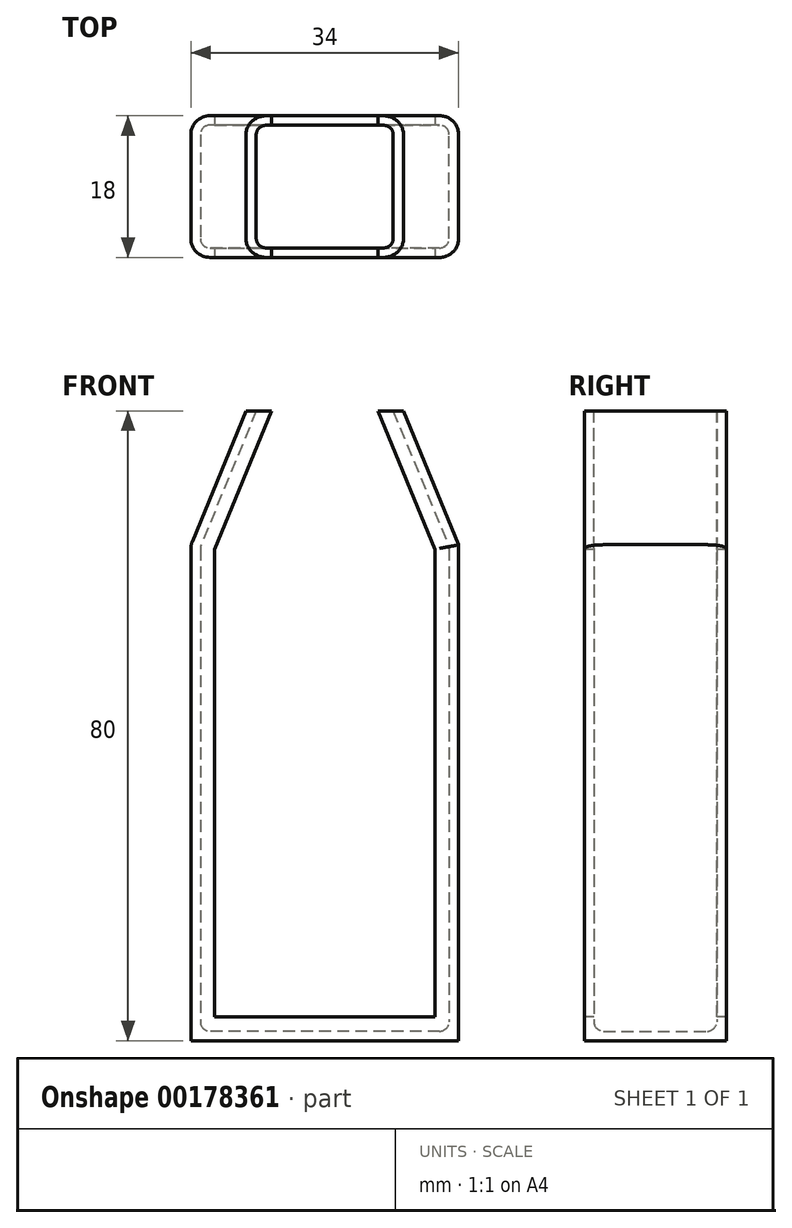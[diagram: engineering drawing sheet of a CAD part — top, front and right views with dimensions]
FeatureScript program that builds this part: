
annotation { "Feature Type Name" : "Feature", "Feature Type Description" : "" }
export const myFeature = defineFeature(function(context is Context, id is Id, definition is map)
    precondition{}
    {
        {
            var Q0;
            Q0=qCreatedBy(makeId("Top.planeOp"),FACE);
            var sketch = newSketch(context, id + "F0", { "sketchPlane" : qUnion([Q0])});
            skLineSegment(sketch, "E0.bottom", {"start": v(17, -9) * mm, "end": v(-17, -9) * mm});
            skLineSegment(sketch, "E0.top", {"start": v(17, 9) * mm, "end": v(-17, 9) * mm});
            skLineSegment(sketch, "E0.left", {"start": v(17, -9) * mm, "end": v(17, 9) * mm});
            skLineSegment(sketch, "E0.right", {"start": v(-17, -9) * mm, "end": v(-17, 9) * mm});
            skPoint(sketch, "E0.middle", {"position": v(0, 0) * mm});
            skSolve(sketch);
        }
        {
            var Q0;
            Q0=makeQuery(id+"F0.imprint","IMPRINT",FACE,{"disambiguationData":[TD([[makeQuery(id+"F0.imprint","IMPRINT",EDGE,{"derivedFrom":sQuery(id+"F0.wireOp",EDGE,"E0.bottom")}),-1.0]])]});
            extrude(context, id + "F1", {"entities" : qUnion([Q0]), "depth" : 80 * mm});
        }
        {
            var Q0;
            Q0=makeQuery(id+"F1.opExtrude","CAP_EDGE",EDGE,{"disambiguationData":[OSD([sQuery(id+"F0.wireOp",EDGE,"E0.right")])],"isStart":false});
            var Q1;
            Q1=makeQuery(id+"F1.opExtrude","CAP_EDGE",EDGE,{"disambiguationData":[OSD([sQuery(id+"F0.wireOp",EDGE,"E0.left")])],"isStart":false});
            chamfer(context, id + "F2", {"entities" : qUnion([Q0, Q1]), "chamferType" : ChamferType.TWO_OFFSETS, "width1" : 17 * mm, "oppositeDirection" : false, "width2" : 7 * mm, "tangentPropagation" : true});
        }
        {
            var Q0;
            Q0=makeQuery(id+"F1.opExtrude","CAP_FACE",FACE,{"disambiguationData":[OSD([sQuery(id+"F0.wireOp",EDGE,"E0.bottom"),sQuery(id+"F0.wireOp",EDGE,"E0.top"),sQuery(id+"F0.wireOp",EDGE,"E0.left"),sQuery(id+"F0.wireOp",EDGE,"E0.right")])],"isStart":false});
            shell(context, id + "F3", {"entities" : qUnion([Q0]), "thickness" : 1.2 * mm});
        }
        {
            var Q0;
            Q0=makeQuery(id+"F1.opExtrude","SWEPT_FACE",FACE,{"disambiguationData":[OSD([sQuery(id+"F0.wireOp",EDGE,"E0.bottom")])]});
            var sketch = newSketch(context, id + "F4", { "sketchPlane" : qUnion([Q0])});
            skLineSegment(sketch, "E1", {"start": v(-14, 80) * mm, "end": v(-14, 3) * mm});
            skLineSegment(sketch, "E2", {"start": v(-14, 3) * mm, "end": v(14, 3) * mm});
            skLineSegment(sketch, "E3", {"start": v(14, 3) * mm, "end": v(14, 80) * mm});
            skLineSegment(sketch, "E4", {"start": v(14, 62.4) * mm, "end": v(6.76, 80) * mm});
            skLineSegment(sketch, "E5", {"start": v(-14, 62.4) * mm, "end": v(-6.76, 80) * mm});
            skSolve(sketch);
        }
        {
            var Q0;
            {var subQ2=sQuery(id+"F4.wireOp",EDGE,"E2");Q0=makeQuery(id+"F4.imprint","IMPRINT",FACE,{"disambiguationData":[TD([[makeQuery(id+"F4.imprint","IMPRINT",EDGE,{"derivedFrom":subQ2}),1.0]])]});}
            extrude(context, id + "F5", {"entities" : qUnion([Q0]), "operationType" : NewBodyOperationType.REMOVE, "endBound" : BoundingType.THROUGH_ALL, "oppositeDirection" : true, "depth" : 1.2 * mm});
        }
        {
            var Q0;
            {var subQ0=sQuery(id+"F0.wireOp",EDGE,"E0.top");Q0=makeQuery(id+"F3.opShell","OFFSET_EDGE",EDGE,{"disambiguationData":[OSD([subQ0]),TDD([makeQuery(id+"F1.opExtrude","CAP_EDGE",EDGE,{"disambiguationData":[OSD([subQ0])],"isStart":true})])]});}
            var Q1;
            {var subQ0=sQuery(id+"F0.wireOp",EDGE,"E0.right");var subQ1=sQuery(id+"F0.wireOp",EDGE,"E0.top");Q1=makeQuery(id+"F3.opShell","OFFSET_EDGE",EDGE,{"disambiguationData":[OSD([subQ1,subQ0]),TDD([makeQuery(id+"F1.opExtrude","SWEPT_EDGE",EDGE,{"disambiguationData":[OSD([subQ1,subQ0])]})])]});}
            var Q2;
            {var subQ0=sQuery(id+"F0.wireOp",EDGE,"E0.right");var subQ1=sQuery(id+"F0.wireOp",EDGE,"E0.bottom");Q2=makeQuery(id+"F3.opShell","OFFSET_EDGE",EDGE,{"disambiguationData":[OSD([subQ1,subQ0]),TDD([makeQuery(id+"F1.opExtrude","SWEPT_EDGE",EDGE,{"disambiguationData":[OSD([subQ1,subQ0])]})])]});}
            var Q3;
            {var subQ0=sQuery(id+"F0.wireOp",EDGE,"E0.top");var subQ1=sQuery(id+"F0.wireOp",EDGE,"E0.right");Q3=makeQuery(id+"F3.opShell","OFFSET_EDGE",EDGE,{"disambiguationData":[OSD([subQ0,subQ1]),TDD([makeQuery(id+"F2.opChamfer","BLEND_EDGE",EDGE,{"blendedFrom":[makeQuery(id+"F1.opExtrude","CAP_EDGE",EDGE,{"disambiguationData":[OSD([subQ1])],"isStart":false}),makeQuery(id+"F1.opExtrude","SWEPT_FACE",FACE,{"disambiguationData":[OSD([subQ0])]})],"blendedInto":[makeQuery(id+"F1.opExtrude","SWEPT_FACE",FACE,{"disambiguationData":[OSD([subQ0])]})]})])]});}
            var Q4;
            {var subQ0=sQuery(id+"F0.wireOp",EDGE,"E0.bottom");var subQ1=sQuery(id+"F0.wireOp",EDGE,"E0.right");Q4=makeQuery(id+"F3.opShell","OFFSET_EDGE",EDGE,{"disambiguationData":[OSD([subQ0,subQ1]),TDD([makeQuery(id+"F2.opChamfer","BLEND_EDGE",EDGE,{"blendedFrom":[makeQuery(id+"F1.opExtrude","CAP_EDGE",EDGE,{"disambiguationData":[OSD([subQ1])],"isStart":false}),makeQuery(id+"F1.opExtrude","SWEPT_FACE",FACE,{"disambiguationData":[OSD([subQ0])]})],"blendedInto":[makeQuery(id+"F1.opExtrude","SWEPT_FACE",FACE,{"disambiguationData":[OSD([subQ0])]})]})])]});}
            var Q5;
            {var subQ0=sQuery(id+"F0.wireOp",EDGE,"E0.left");var subQ1=sQuery(id+"F0.wireOp",EDGE,"E0.bottom");Q5=makeQuery(id+"F3.opShell","OFFSET_EDGE",EDGE,{"disambiguationData":[OSD([subQ1,subQ0]),TDD([makeQuery(id+"F1.opExtrude","SWEPT_EDGE",EDGE,{"disambiguationData":[OSD([subQ1,subQ0])]})])]});}
            var Q6;
            {var subQ0=sQuery(id+"F0.wireOp",EDGE,"E0.bottom");var subQ1=sQuery(id+"F0.wireOp",EDGE,"E0.left");Q6=makeQuery(id+"F3.opShell","OFFSET_EDGE",EDGE,{"disambiguationData":[OSD([subQ0,subQ1]),TDD([makeQuery(id+"F2.opChamfer","BLEND_EDGE",EDGE,{"blendedFrom":[makeQuery(id+"F1.opExtrude","CAP_EDGE",EDGE,{"disambiguationData":[OSD([subQ1])],"isStart":false}),makeQuery(id+"F1.opExtrude","SWEPT_FACE",FACE,{"disambiguationData":[OSD([subQ0])]})],"blendedInto":[makeQuery(id+"F1.opExtrude","SWEPT_FACE",FACE,{"disambiguationData":[OSD([subQ0])]})]})])]});}
            var Q7;
            {var subQ0=sQuery(id+"F0.wireOp",EDGE,"E0.left");Q7=makeQuery(id+"F3.opShell","OFFSET_EDGE",EDGE,{"disambiguationData":[OSD([subQ0]),TDD([makeQuery(id+"F2.opChamfer","BLEND_EDGE",EDGE,{"blendedFrom":[makeQuery(id+"F1.opExtrude","CAP_EDGE",EDGE,{"disambiguationData":[OSD([subQ0])],"isStart":false}),makeQuery(id+"F1.opExtrude","SWEPT_FACE",FACE,{"disambiguationData":[OSD([subQ0])]})],"blendedInto":[makeQuery(id+"F1.opExtrude","SWEPT_FACE",FACE,{"disambiguationData":[OSD([subQ0])]})]})])]});}
            var Q8;
            {var subQ0=sQuery(id+"F0.wireOp",EDGE,"E0.left");var subQ1=sQuery(id+"F0.wireOp",EDGE,"E0.top");Q8=makeQuery(id+"F3.opShell","OFFSET_EDGE",EDGE,{"disambiguationData":[OSD([subQ1,subQ0]),TDD([makeQuery(id+"F1.opExtrude","SWEPT_EDGE",EDGE,{"disambiguationData":[OSD([subQ1,subQ0])]})])]});}
            var Q9;
            {var subQ0=sQuery(id+"F0.wireOp",EDGE,"E0.top");var subQ1=sQuery(id+"F0.wireOp",EDGE,"E0.left");Q9=makeQuery(id+"F3.opShell","OFFSET_EDGE",EDGE,{"disambiguationData":[OSD([subQ0,subQ1]),TDD([makeQuery(id+"F2.opChamfer","BLEND_EDGE",EDGE,{"blendedFrom":[makeQuery(id+"F1.opExtrude","CAP_EDGE",EDGE,{"disambiguationData":[OSD([subQ1])],"isStart":false}),makeQuery(id+"F1.opExtrude","SWEPT_FACE",FACE,{"disambiguationData":[OSD([subQ0])]})],"blendedInto":[makeQuery(id+"F1.opExtrude","SWEPT_FACE",FACE,{"disambiguationData":[OSD([subQ0])]})]})])]});}
            var Q10;
            {var subQ0=sQuery(id+"F0.wireOp",EDGE,"E0.left");Q10=makeQuery(id+"F3.opShell","OFFSET_EDGE",EDGE,{"disambiguationData":[OSD([subQ0]),TDD([makeQuery(id+"F1.opExtrude","CAP_EDGE",EDGE,{"disambiguationData":[OSD([subQ0])],"isStart":true})])]});}
            var Q11;
            {var subQ0=sQuery(id+"F0.wireOp",EDGE,"E0.right");Q11=makeQuery(id+"F3.opShell","OFFSET_EDGE",EDGE,{"disambiguationData":[OSD([subQ0]),TDD([makeQuery(id+"F1.opExtrude","CAP_EDGE",EDGE,{"disambiguationData":[OSD([subQ0])],"isStart":true})])]});}
            var Q12;
            {var subQ0=sQuery(id+"F0.wireOp",EDGE,"E0.right");Q12=makeQuery(id+"F3.opShell","OFFSET_EDGE",EDGE,{"disambiguationData":[OSD([subQ0]),TDD([makeQuery(id+"F2.opChamfer","BLEND_EDGE",EDGE,{"blendedFrom":[makeQuery(id+"F1.opExtrude","CAP_EDGE",EDGE,{"disambiguationData":[OSD([subQ0])],"isStart":false}),makeQuery(id+"F1.opExtrude","SWEPT_FACE",FACE,{"disambiguationData":[OSD([subQ0])]})],"blendedInto":[makeQuery(id+"F1.opExtrude","SWEPT_FACE",FACE,{"disambiguationData":[OSD([subQ0])]})]})])]});}
            var Q13;
            {var subQ0=sQuery(id+"F0.wireOp",EDGE,"E0.bottom");Q13=makeQuery(id+"F3.opShell","OFFSET_EDGE",EDGE,{"disambiguationData":[OSD([subQ0]),TDD([makeQuery(id+"F1.opExtrude","CAP_EDGE",EDGE,{"disambiguationData":[OSD([subQ0])],"isStart":true})])]});}
            fillet(context, id + "F6", {"entities" : qUnion([Q0, Q1, Q2, Q3, Q4, Q5, Q6, Q7, Q8, Q9, Q10, Q11, Q12, Q13]), "radius" : 1.2 * mm, "tangentPropagation" : true, "allowEdgeOverflow" : false});
        }
        {
            var Q0;
            Q0=makeQuery(id+"F1.opExtrude","SWEPT_EDGE",EDGE,{"disambiguationData":[OSD([sQuery(id+"F0.wireOp",EDGE,"E0.top"),sQuery(id+"F0.wireOp",EDGE,"E0.right")])]});
            var Q1;
            Q1=makeQuery(id+"F1.opExtrude","SWEPT_EDGE",EDGE,{"disambiguationData":[OSD([sQuery(id+"F0.wireOp",EDGE,"E0.top"),sQuery(id+"F0.wireOp",EDGE,"E0.left")])]});
            var Q2;
            Q2=makeQuery(id+"F1.opExtrude","SWEPT_EDGE",EDGE,{"disambiguationData":[OSD([sQuery(id+"F0.wireOp",EDGE,"E0.bottom"),sQuery(id+"F0.wireOp",EDGE,"E0.right")])]});
            var Q3;
            Q3=makeQuery(id+"F2.opChamfer","BLEND_EDGE",EDGE,{"blendedFrom":[makeQuery(id+"F1.opExtrude","CAP_EDGE",EDGE,{"disambiguationData":[OSD([sQuery(id+"F0.wireOp",EDGE,"E0.right")])],"isStart":false}),makeQuery(id+"F1.opExtrude","SWEPT_FACE",FACE,{"disambiguationData":[OSD([sQuery(id+"F0.wireOp",EDGE,"E0.top")])]})],"blendedInto":[makeQuery(id+"F1.opExtrude","SWEPT_FACE",FACE,{"disambiguationData":[OSD([sQuery(id+"F0.wireOp",EDGE,"E0.top")])]})]});
            var Q4;
            {var subQ0=sQuery(id+"F0.wireOp",EDGE,"E0.right");Q4=makeQuery(id+"F2.opChamfer","BLEND_EDGE",EDGE,{"blendedFrom":[makeQuery(id+"F1.opExtrude","CAP_EDGE",EDGE,{"disambiguationData":[OSD([subQ0])],"isStart":false}),makeQuery(id+"F1.opExtrude","SWEPT_FACE",FACE,{"disambiguationData":[OSD([subQ0])]})],"blendedInto":[makeQuery(id+"F1.opExtrude","SWEPT_FACE",FACE,{"disambiguationData":[OSD([subQ0])]})]});}
            var Q5;
            Q5=makeQuery(id+"F2.opChamfer","BLEND_EDGE",EDGE,{"blendedFrom":[makeQuery(id+"F1.opExtrude","CAP_EDGE",EDGE,{"disambiguationData":[OSD([sQuery(id+"F0.wireOp",EDGE,"E0.right")])],"isStart":false}),makeQuery(id+"F1.opExtrude","SWEPT_FACE",FACE,{"disambiguationData":[OSD([sQuery(id+"F0.wireOp",EDGE,"E0.bottom")])]})],"blendedInto":[makeQuery(id+"F1.opExtrude","SWEPT_FACE",FACE,{"disambiguationData":[OSD([sQuery(id+"F0.wireOp",EDGE,"E0.bottom")])]})]});
            var Q6;
            Q6=makeQuery(id+"F2.opChamfer","BLEND_EDGE",EDGE,{"blendedFrom":[makeQuery(id+"F1.opExtrude","CAP_EDGE",EDGE,{"disambiguationData":[OSD([sQuery(id+"F0.wireOp",EDGE,"E0.left")])],"isStart":false}),makeQuery(id+"F1.opExtrude","SWEPT_FACE",FACE,{"disambiguationData":[OSD([sQuery(id+"F0.wireOp",EDGE,"E0.bottom")])]})],"blendedInto":[makeQuery(id+"F1.opExtrude","SWEPT_FACE",FACE,{"disambiguationData":[OSD([sQuery(id+"F0.wireOp",EDGE,"E0.bottom")])]})]});
            var Q7;
            Q7=makeQuery(id+"F1.opExtrude","SWEPT_EDGE",EDGE,{"disambiguationData":[OSD([sQuery(id+"F0.wireOp",EDGE,"E0.bottom"),sQuery(id+"F0.wireOp",EDGE,"E0.left")])]});
            var Q8;
            Q8=makeQuery(id+"F2.opChamfer","BLEND_EDGE",EDGE,{"blendedFrom":[makeQuery(id+"F1.opExtrude","CAP_EDGE",EDGE,{"disambiguationData":[OSD([sQuery(id+"F0.wireOp",EDGE,"E0.left")])],"isStart":false}),makeQuery(id+"F1.opExtrude","SWEPT_FACE",FACE,{"disambiguationData":[OSD([sQuery(id+"F0.wireOp",EDGE,"E0.top")])]})],"blendedInto":[makeQuery(id+"F1.opExtrude","SWEPT_FACE",FACE,{"disambiguationData":[OSD([sQuery(id+"F0.wireOp",EDGE,"E0.top")])]})]});
            fillet(context, id + "F7", {"entities" : qUnion([Q0, Q1, Q2, Q3, Q4, Q5, Q6, Q7, Q8]), "radius" : 2.4 * mm, "tangentPropagation" : true, "allowEdgeOverflow" : false});
        }
    });
